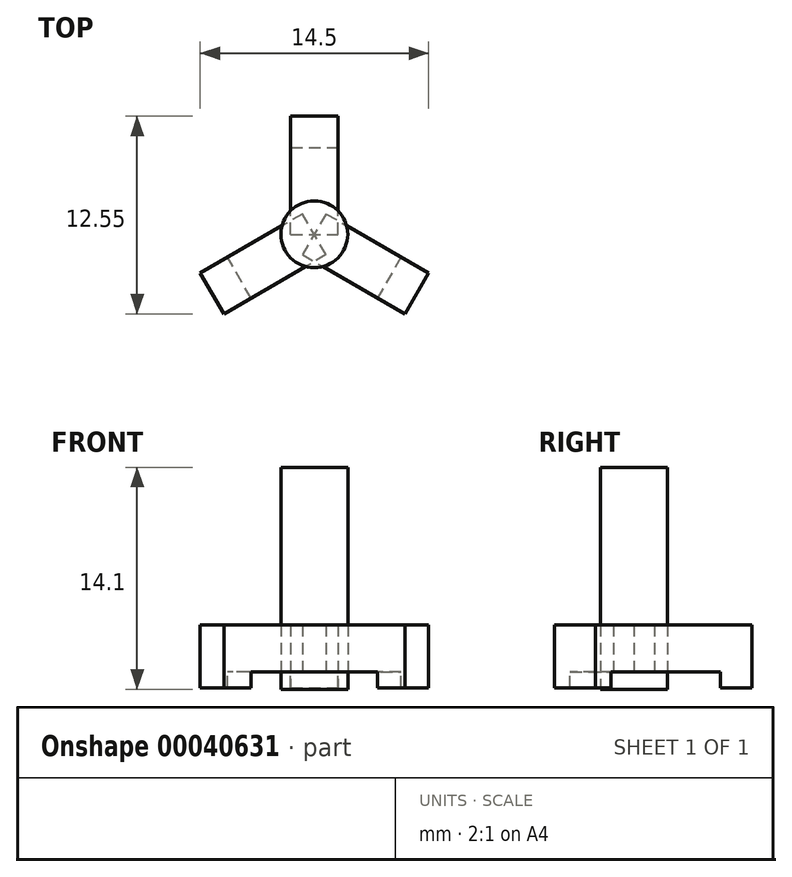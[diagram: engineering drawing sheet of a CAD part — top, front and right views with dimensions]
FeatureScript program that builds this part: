
annotation { "Feature Type Name" : "Feature", "Feature Type Description" : "" }
export const myFeature = defineFeature(function(context is Context, id is Id, definition is map)
    precondition{}
    {
        {
            var Q0;
            Q0=qCreatedBy(makeId("Top.planeOp"),FACE);
            var sketch = newSketch(context, id + "F0", { "sketchPlane" : qUnion([Q0])});
            skLineSegment(sketch, "E0.bottom", {"start": v(-1.5, 0) * mm, "end": v(1.5, 0) * mm});
            skLineSegment(sketch, "E0.top", {"start": v(-1.5, 7.5) * mm, "end": v(1.5, 7.5) * mm});
            skLineSegment(sketch, "E0.left", {"start": v(-1.5, 0) * mm, "end": v(-1.5, 7.5) * mm});
            skLineSegment(sketch, "E0.right", {"start": v(1.5, 0) * mm, "end": v(1.5, 7.5) * mm});
            skSolve(sketch);
        }
        {
            var Q0;
            Q0=makeQuery(id+"F0.imprint","IMPRINT",FACE,{"disambiguationData":[TD([[makeQuery(id+"F0.imprint","IMPRINT",EDGE,{"derivedFrom":sQuery(id+"F0.wireOp",EDGE,"E0.bottom")}),1.0]])]});
            extrude(context, id + "F1", {"entities" : qUnion([Q0]), "depth" : 3 * mm});
        }
        {
            var Q0;
            Q0=makeQuery(id+"F1.opExtrude","CAP_FACE",FACE,{"disambiguationData":[OSD([sQuery(id+"F0.wireOp",EDGE,"E0.bottom"),sQuery(id+"F0.wireOp",EDGE,"E0.top"),sQuery(id+"F0.wireOp",EDGE,"E0.left"),sQuery(id+"F0.wireOp",EDGE,"E0.right")])],"isStart":true});
            var sketch = newSketch(context, id + "F2", { "sketchPlane" : qUnion([Q0])});
            skLineSegment(sketch, "E1.bottom", {"start": v(-1.5, -7.5) * mm, "end": v(1.5, -7.5) * mm});
            skLineSegment(sketch, "E1.top", {"start": v(-1.5, -5.5) * mm, "end": v(1.5, -5.5) * mm});
            skLineSegment(sketch, "E1.left", {"start": v(-1.5, -7.5) * mm, "end": v(-1.5, -5.5) * mm});
            skLineSegment(sketch, "E1.right", {"start": v(1.5, -7.5) * mm, "end": v(1.5, -5.5) * mm});
            skSolve(sketch);
        }
        {
            var Q0;
            Q0=makeQuery(id+"F2.imprint","IMPRINT",FACE,{"disambiguationData":[TD([[makeQuery(id+"F2.imprint","IMPRINT",EDGE,{"derivedFrom":sQuery(id+"F2.wireOp",EDGE,"E1.bottom")}),1.0]])]});
            extrude(context, id + "F3", {"entities" : qUnion([Q0]), "operationType" : NewBodyOperationType.ADD, "depth" : 1 * mm});
        }
        {
            var Q0;
            Q0=qCreatedBy(makeId("Right.planeOp"),FACE);
            var sketch = newSketch(context, id + "F4", { "sketchPlane" : qUnion([Q0])});
            skLineSegment(sketch, "E2", {"start": v(0, 45.63) * mm, "end": v(0, -38.13) * mm, "construction": true});
            skSolve(sketch);
        }
        {
            var Q0;
            Q0=makeQuery(id+"F1.opExtrude","SWEPT_BODY",BODY,{"disambiguationData":[OSD([sQuery(id+"F0.wireOp",EDGE,"E0.bottom"),sQuery(id+"F0.wireOp",EDGE,"E0.top"),sQuery(id+"F0.wireOp",EDGE,"E0.left"),sQuery(id+"F0.wireOp",EDGE,"E0.right")])]});
            var Q1;
            Q1=sQuery(id+"F4.wireOp",EDGE,"E2");
            circularPattern(context, id + "F5", {"entities" : qUnion([Q0]), "axis" : qUnion([Q1]), "angle" : 360 * degree, "instanceCount" : 3, "oppositeDirection" : true, "equalSpace" : true});
        }
        {
            var Q0;
            Q0=makeQuery(id+"F1.opExtrude","CAP_FACE",FACE,{"disambiguationData":[OSD([sQuery(id+"F0.wireOp",EDGE,"E0.bottom"),sQuery(id+"F0.wireOp",EDGE,"E0.top"),sQuery(id+"F0.wireOp",EDGE,"E0.left"),sQuery(id+"F0.wireOp",EDGE,"E0.right")])],"isStart":false});
            var sketch = newSketch(context, id + "F6", { "sketchPlane" : qUnion([Q0])});
            skCircle(sketch, "E3", {"center": v(0, 0) * mm, "radius": 2.12 * mm});
            skSolve(sketch);
        }
        {
            var Q0;
            Q0 = qSketchRegion(id + "F6", true);
            extrude(context, id + "F7", {"entities" : qUnion([Q0]), "depth" : 10 * mm, "hasSecondDirection" : true, "secondDirectionOppositeDirection" : true, "secondDirectionDepth" : 4.1 * mm});
        }
    });
